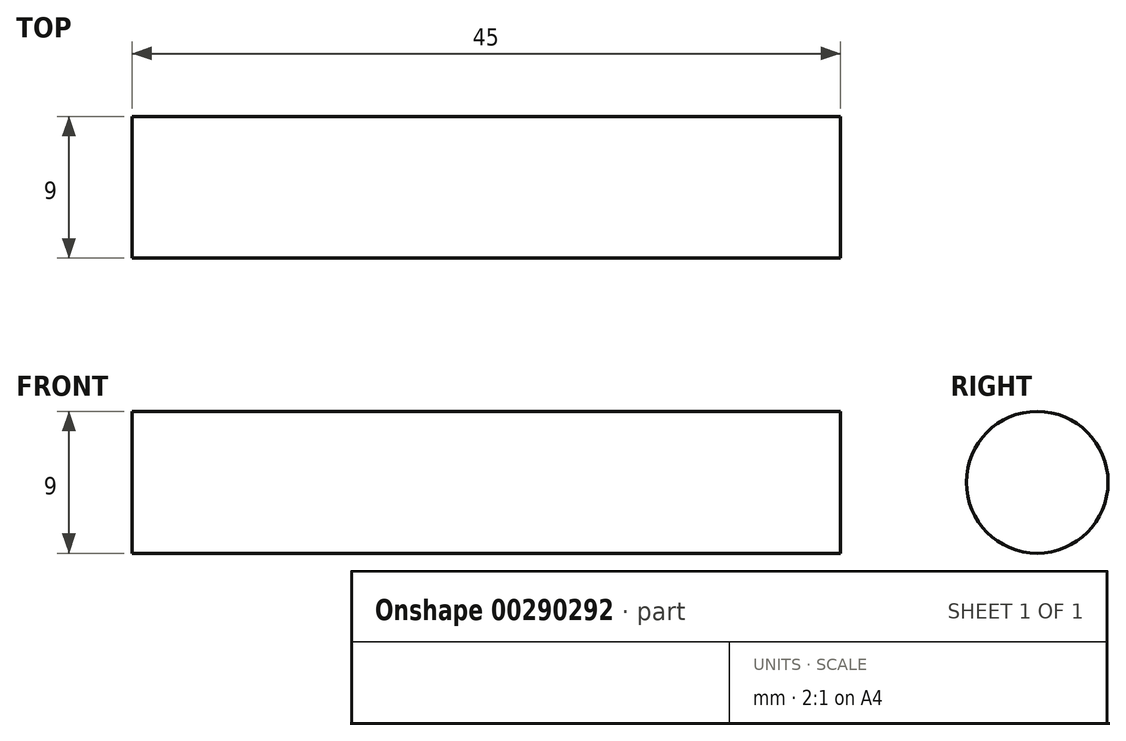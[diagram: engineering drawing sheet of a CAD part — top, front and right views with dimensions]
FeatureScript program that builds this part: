
annotation { "Feature Type Name" : "Feature", "Feature Type Description" : "" }
export const myFeature = defineFeature(function(context is Context, id is Id, definition is map)
    precondition{}
    {
        {
            var Q0;
            Q0=qCreatedBy(makeId("Front.planeOp"),FACE);
            var sketch = newSketch(context, id + "F0", { "sketchPlane" : qUnion([Q0])});
            skLineSegment(sketch, "E0", {"start": v(0, 4.5) * mm, "end": v(22.5, 4.5) * mm});
            skLineSegment(sketch, "E1", {"start": v(22.5, 4.5) * mm, "end": v(22.5, 0) * mm});
            skLineSegment(sketch, "E2.MirrorCS", {"start": v(0, 4.5) * mm, "end": v(-22.5, 4.5) * mm});
            skLineSegment(sketch, "E3.MirrorCS", {"start": v(-22.5, 4.5) * mm, "end": v(-22.5, 0) * mm});
            skLineSegment(sketch, "E4", {"start": v(-22.5, 0) * mm, "end": v(22.5, 0) * mm});
            skSolve(sketch);
        }
        {
            var Q0;
            Q0 = qSketchRegion(id + "F0", true);
            var Q1;
            Q1=sQuery(id+"F0.wireOp",EDGE,"E4");
            revolve(context, id + "F1", {"entities" : qUnion([Q0]), "axis" : qUnion([Q1]), "revolveType" : RevolveType.FULL});
        }
    });
